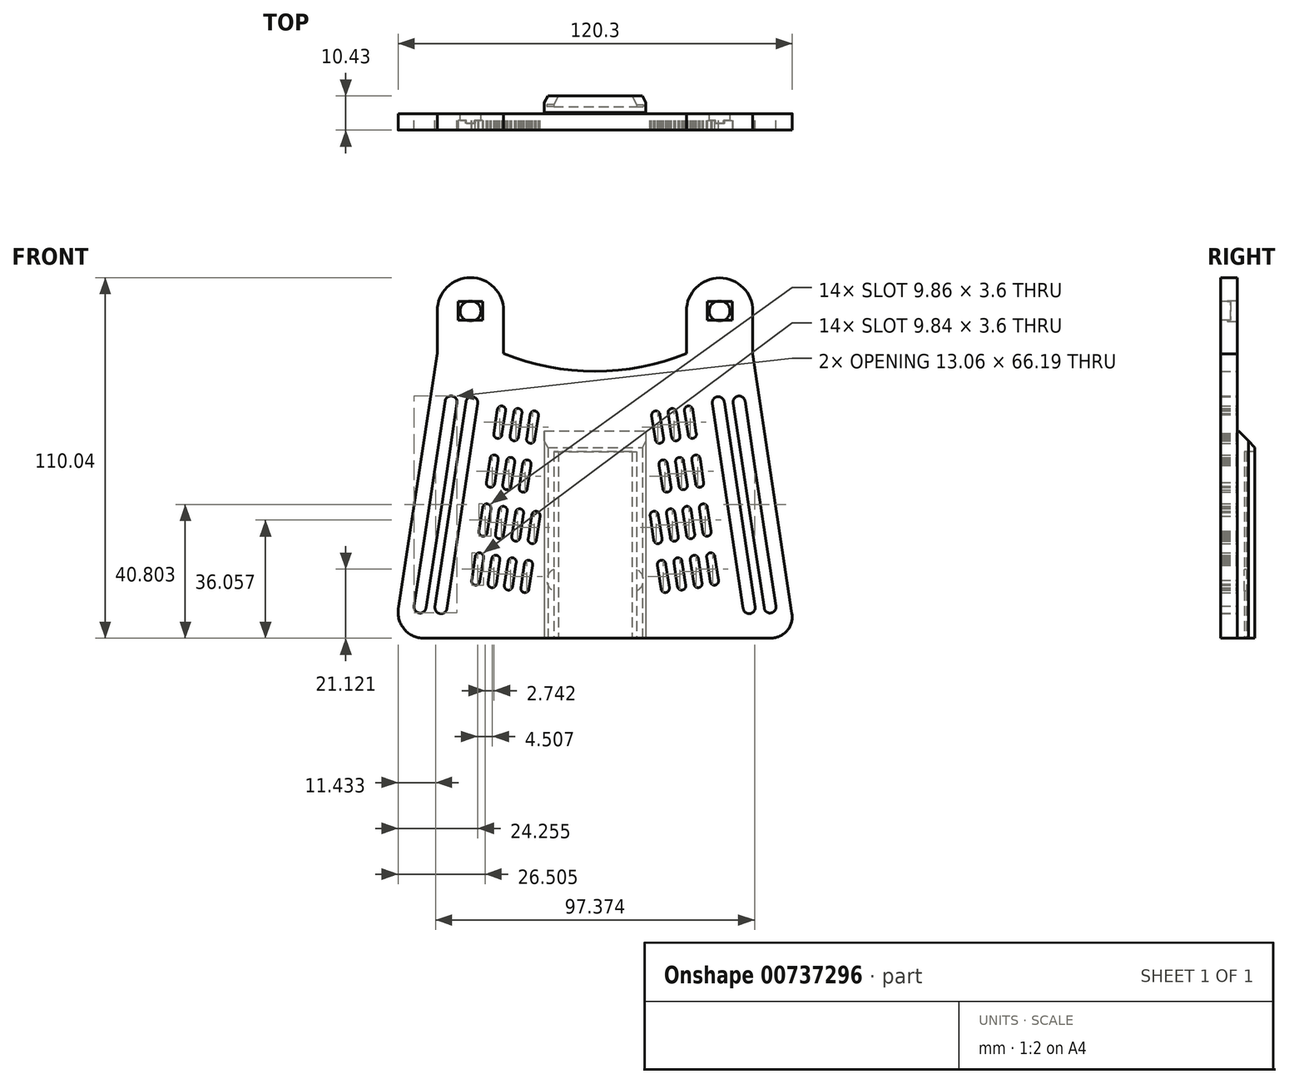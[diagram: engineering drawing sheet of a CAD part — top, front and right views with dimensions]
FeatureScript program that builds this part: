
annotation { "Feature Type Name" : "Feature", "Feature Type Description" : "" }
export const myFeature = defineFeature(function(context is Context, id is Id, definition is map)
    precondition{}
    {
        {
            assignVariable(context, id + "F0", {"name" : "thickness", "anyValue" : 4});
        }
        {
            var Q0;
            Q0=qCreatedBy(makeId("Front.planeOp"),FACE);
            var sketch = newSketch(context, id + "F1", { "sketchPlane" : qUnion([Q0])});
            skLineSegment(sketch, "E0", {"start": v(-22.08, 35.56) * mm, "end": v(-22.08, 25.27) * mm});
            skLineSegment(sketch, "E1", {"start": v(-38.08, 35.56) * mm, "end": v(-38.08, 25.41) * mm});
            skLineSegment(sketch, "E2", {"start": v(-38.08, 25.41) * mm, "end": v(-47.46, -36.33) * mm});
            skLineSegment(sketch, "E3", {"start": v(-41.36, -43.42) * mm, "end": v(42.4, -43.42) * mm});
            skLineSegment(sketch, "E4", {"start": v(47.52, -37.48) * mm, "end": v(38.06, 25.2) * mm});
            skLineSegment(sketch, "E5", {"start": v(38.06, 25.2) * mm, "end": v(38.06, 35.5) * mm});
            skLineSegment(sketch, "E6", {"start": v(22.06, 35.5) * mm, "end": v(22.06, 25.26) * mm});
            skArc(sketch, "E7", {"start": v(-22.08, 25.27) * mm, "mid": v(0, 21) * mm, "end": v(22.06, 25.26) * mm});
            skCircle(sketch, "E8", {"center": v(-30.08, 35.56) * mm, "radius": 8 * mm});
            skPoint(sketch, "E8.first.point", {"position": v(-30.38, 43.56) * mm});
            skCircle(sketch, "E9", {"center": v(30.06, 35.5) * mm, "radius": 8 * mm});
            skPoint(sketch, "E9.second.point", {"position": v(29.54, 43.49) * mm});
            skArc(sketch, "E10", {"start": v(47.52, -37.48) * mm, "mid": v(46.33, -41.63) * mm, "end": v(42.4, -43.42) * mm});
            skArc(sketch, "E11", {"start": v(-47.46, -36.33) * mm, "mid": v(-46.04, -41.28) * mm, "end": v(-41.36, -43.42) * mm});
            skLineSegment(sketch, "E12", {"start": v(0, 64.8) * mm, "end": v(0, 21) * mm, "construction": true});
            skLineSegment(sketch, "E13", {"start": v(0, 21) * mm, "end": v(0, -58.54) * mm, "construction": true});
            skCircle(sketch, "E14", {"center": v(34.76, 13.56) * mm, "radius": 1.45 * mm});
            skPoint(sketch, "E14.first.point", {"position": v(33.33, 13.34) * mm});
            skPoint(sketch, "E14.second.point", {"position": v(34.45, 14.97) * mm});
            skPoint(sketch, "E14.third.point", {"position": v(36.2, 13.77) * mm});
            skPoint(sketch, "E15.first.point", {"position": v(35.7, -2.5) * mm});
            skPoint(sketch, "E15.second.point", {"position": v(38.57, -2.07) * mm});
            skPoint(sketch, "E16.first.point", {"position": v(38.32, -19.78) * mm});
            skPoint(sketch, "E16.third.point", {"position": v(41.17, -19.34) * mm});
            skLineSegment(sketch, "E17", {"start": v(43.34, -43.34) * mm, "end": v(30.24, 43.5) * mm, "construction": true});
            skCircle(sketch, "E18", {"center": v(42.23, -35.9) * mm, "radius": 1.45 * mm});
            skPoint(sketch, "E18.first.point", {"position": v(40.8, -36.12) * mm});
            skPoint(sketch, "E18.second.point", {"position": v(42.44, -37.33) * mm});
            skPoint(sketch, "E18.third.point", {"position": v(43.67, -35.74) * mm});
            skLineSegment(sketch, "E19", {"start": v(36.2, 13.77) * mm, "end": v(38.57, -2.07) * mm});
            skLineSegment(sketch, "E20", {"start": v(33.33, 13.34) * mm, "end": v(35.7, -2.5) * mm});
            skLineSegment(sketch, "E21", {"start": v(38.32, -19.78) * mm, "end": v(40.8, -36.12) * mm});
            skLineSegment(sketch, "E22", {"start": v(41.17, -19.34) * mm, "end": v(43.67, -35.74) * mm});
            skLineSegment(sketch, "E23", {"start": v(41.17, -19.34) * mm, "end": v(38.57, -2.07) * mm});
            skLineSegment(sketch, "E24", {"start": v(38.32, -19.78) * mm, "end": v(35.7, -2.5) * mm});
            skLineSegment(sketch, "E25", {"start": v(30.88, -43.42) * mm, "end": v(20.6, 24.7) * mm, "construction": true});
            skCircle(sketch, "E26", {"center": v(28.8, -29.63) * mm, "radius": 1 * mm});
            skLineSegment(sketch, "E27", {"start": v(26.92, -23.82) * mm, "end": v(27.8, -29.78) * mm});
            skLineSegment(sketch, "E28", {"start": v(28.9, -23.6) * mm, "end": v(29.8, -29.53) * mm});
            skCircle(sketch, "E29", {"center": v(27.92, -23.82) * mm, "radius": 1 * mm});
            skLineSegment(sketch, "E30", {"start": v(29.25, -32.63) * mm, "end": v(35.1, -31.75) * mm, "construction": true});
            skLineSegment(sketch, "E31", {"start": v(27.47, -20.82) * mm, "end": v(32.3, -20.1) * mm, "construction": true});
            skCircle(sketch, "E32.MirrorC", {"center": v(24.36, -0.2) * mm, "radius": 1 * mm});
            skLineSegment(sketch, "E33.MirrorCS", {"start": v(25.33, 0.02) * mm, "end": v(26.23, -5.91) * mm});
            skLineSegment(sketch, "E34.MirrorCS", {"start": v(23.36, -0.2) * mm, "end": v(24.24, -6.16) * mm});
            skCircle(sketch, "E35.MirrorC", {"center": v(25.23, -6.01) * mm, "radius": 1 * mm});
            skCircle(sketch, "E36.MirrorC", {"center": v(27.01, -17.82) * mm, "radius": 1 * mm});
            skCircle(sketch, "E37.MirrorC", {"center": v(26.14, -12.01) * mm, "radius": 1 * mm});
            skLineSegment(sketch, "E38.MirrorCS", {"start": v(26.06, -18.12) * mm, "end": v(25.15, -12.17) * mm});
            skLineSegment(sketch, "E39.MirrorCS", {"start": v(28.01, -17.75) * mm, "end": v(27.12, -11.82) * mm});
            skLineSegment(sketch, "E40", {"start": v(23.9, 2.8) * mm, "end": v(29.03, 3.57) * mm, "construction": true});
            skCircle(sketch, "E41.MirrorC", {"center": v(22.58, 11.6) * mm, "radius": 1 * mm});
            skCircle(sketch, "E42.MirrorC", {"center": v(23.45, 5.8) * mm, "radius": 1 * mm});
            skLineSegment(sketch, "E43.MirrorCS", {"start": v(24.45, 5.86) * mm, "end": v(23.56, 11.8) * mm});
            skLineSegment(sketch, "E44.MirrorCS", {"start": v(22.5, 5.5) * mm, "end": v(21.59, 11.45) * mm});
            skCircle(sketch, "E45", {"center": v(29.73, 13.4) * mm, "radius": 1.45 * mm});
            skPoint(sketch, "E45.first.point", {"position": v(28.3, 13.18) * mm});
            skPoint(sketch, "E45.second.point", {"position": v(29.41, 14.81) * mm});
            skPoint(sketch, "E45.third.point", {"position": v(31.16, 13.61) * mm});
            skLineSegment(sketch, "E46", {"start": v(38.31, -43.5) * mm, "end": v(25.21, 43.34) * mm, "construction": true});
            skCircle(sketch, "E47", {"center": v(37.2, -36.06) * mm, "radius": 1.45 * mm});
            skLineSegment(sketch, "E48", {"start": v(28.85, -43.42) * mm, "end": v(18.68, 24.02) * mm, "construction": true});
            skCircle(sketch, "E49.MirrorC", {"center": v(22.18, -12.61) * mm, "radius": 1 * mm});
            skCircle(sketch, "E50.MirrorC", {"center": v(21.28, -6.61) * mm, "radius": 1 * mm});
            skCircle(sketch, "E51.MirrorC", {"center": v(18.62, 11) * mm, "radius": 1 * mm});
            skCircle(sketch, "E52.MirrorC", {"center": v(19.5, 5.2) * mm, "radius": 1 * mm});
            skLineSegment(sketch, "E53.MirrorCS", {"start": v(18.52, 4.97) * mm, "end": v(17.63, 10.9) * mm});
            skLineSegment(sketch, "E54.MirrorCS", {"start": v(19.95, 2.2) * mm, "end": v(14.82, 1.42) * mm, "construction": true});
            skLineSegment(sketch, "E55.MirrorCS", {"start": v(25.3, -33.23) * mm, "end": v(19.45, -34.1) * mm, "construction": true});
            skCircle(sketch, "E56.MirrorC", {"center": v(20.4, -0.8) * mm, "radius": 1 * mm});
            skCircle(sketch, "E57.MirrorC", {"center": v(23.96, -24.42) * mm, "radius": 1 * mm});
            skLineSegment(sketch, "E58.MirrorCS", {"start": v(26.92, -44.02) * mm, "end": v(16.64, 24.1) * mm, "construction": true});
            skLineSegment(sketch, "E59.MirrorCS", {"start": v(23.51, -21.42) * mm, "end": v(18.69, -22.15) * mm, "construction": true});
            skCircle(sketch, "E60.MirrorC", {"center": v(23.06, -18.42) * mm, "radius": 1 * mm});
            skCircle(sketch, "E61.MirrorC", {"center": v(24.84, -30.23) * mm, "radius": 1 * mm});
            skLineSegment(sketch, "E62.MirrorCS", {"start": v(19.4, -0.87) * mm, "end": v(20.3, -6.8) * mm});
            skLineSegment(sketch, "E63.MirrorCS", {"start": v(21.36, -0.5) * mm, "end": v(22.27, -6.46) * mm});
            skLineSegment(sketch, "E64.MirrorCS", {"start": v(24.92, -24.12) * mm, "end": v(25.83, -30.07) * mm});
            skLineSegment(sketch, "E65.MirrorCS", {"start": v(20.5, 5.2) * mm, "end": v(19.6, 11.15) * mm});
            skLineSegment(sketch, "E66.MirrorCS", {"start": v(22.97, -24.49) * mm, "end": v(23.86, -30.42) * mm});
            skLineSegment(sketch, "E67.MirrorCS", {"start": v(24.06, -18.42) * mm, "end": v(23.17, -12.46) * mm});
            skLineSegment(sketch, "E68.MirrorCS", {"start": v(22.09, -18.65) * mm, "end": v(21.19, -12.71) * mm});
            skLineSegment(sketch, "E69", {"start": v(28.3, 13.18) * mm, "end": v(35.76, -36.28) * mm});
            skLineSegment(sketch, "E70", {"start": v(31.16, 13.61) * mm, "end": v(38.62, -35.85) * mm});
            skLineSegment(sketch, "E71", {"start": v(14.8, 22.88) * mm, "end": v(24.8, -43.42) * mm, "construction": true});
            skCircle(sketch, "E72.MirrorC", {"center": v(18.23, -13.2) * mm, "radius": 1 * mm});
            skCircle(sketch, "E73.MirrorC", {"center": v(16.45, -1.4) * mm, "radius": 1 * mm});
            skCircle(sketch, "E74.MirrorC", {"center": v(14.67, 10.4) * mm, "radius": 1 * mm});
            skCircle(sketch, "E75.MirrorC", {"center": v(15.54, 4.6) * mm, "radius": 1 * mm});
            skCircle(sketch, "E76.MirrorC", {"center": v(20.89, -30.82) * mm, "radius": 1 * mm});
            skCircle(sketch, "E77.MirrorC", {"center": v(20, -25.02) * mm, "radius": 1 * mm});
            skLineSegment(sketch, "E78.MirrorCS", {"start": v(15.6, -22.61) * mm, "end": v(10.78, -23.34) * mm, "construction": true});
            skCircle(sketch, "E79.MirrorC", {"center": v(19.1, -19.02) * mm, "radius": 1 * mm});
            skCircle(sketch, "E80.MirrorC", {"center": v(14.27, -13.8) * mm, "radius": 1 * mm});
            skCircle(sketch, "E81.MirrorC", {"center": v(16.93, -31.42) * mm, "radius": 1 * mm});
            skCircle(sketch, "E82.MirrorC", {"center": v(15.15, -19.61) * mm, "radius": 1 * mm});
            skCircle(sketch, "E83.MirrorC", {"center": v(16.05, -25.61) * mm, "radius": 1 * mm});
            skCircle(sketch, "E84.MirrorC", {"center": v(17.32, -7.2) * mm, "radius": 1 * mm});
            skLineSegment(sketch, "E85.MirrorCS", {"start": v(17, -25.32) * mm, "end": v(17.92, -31.27) * mm});
            skLineSegment(sketch, "E86.MirrorCS", {"start": v(20.1, -18.95) * mm, "end": v(19.2, -13.01) * mm});
            skLineSegment(sketch, "E87.MirrorCS", {"start": v(14.18, -19.84) * mm, "end": v(13.28, -13.9) * mm});
            skLineSegment(sketch, "E88.MirrorCS", {"start": v(18.15, -19.31) * mm, "end": v(17.24, -13.36) * mm});
            skLineSegment(sketch, "E89.MirrorCS", {"start": v(16.15, -19.61) * mm, "end": v(15.26, -13.66) * mm});
            skLineSegment(sketch, "E90.MirrorCS", {"start": v(16, 1.6) * mm, "end": v(21.12, 2.37) * mm, "construction": true});
            skLineSegment(sketch, "E91.MirrorCS", {"start": v(15.45, -1.4) * mm, "end": v(16.33, -7.36) * mm});
            skLineSegment(sketch, "E92.MirrorCS", {"start": v(19, -25.02) * mm, "end": v(19.9, -30.97) * mm});
            skLineSegment(sketch, "E93.MirrorCS", {"start": v(14.59, 4.3) * mm, "end": v(13.68, 10.25) * mm});
            skLineSegment(sketch, "E94.MirrorCS", {"start": v(19.56, -22.02) * mm, "end": v(24.38, -21.29) * mm, "construction": true});
            skLineSegment(sketch, "E95.MirrorCS", {"start": v(20.98, -24.79) * mm, "end": v(21.88, -30.72) * mm});
            skLineSegment(sketch, "E96.MirrorCS", {"start": v(15.06, -25.68) * mm, "end": v(15.95, -31.61) * mm});
            skLineSegment(sketch, "E97.MirrorCS", {"start": v(17.42, -1.17) * mm, "end": v(18.32, -7.1) * mm});
            skLineSegment(sketch, "E98.MirrorCS", {"start": v(19.01, -45.21) * mm, "end": v(8.73, 22.9) * mm, "construction": true});
            skLineSegment(sketch, "E99.MirrorCS", {"start": v(12.04, 1) * mm, "end": v(6.91, 0.23) * mm, "construction": true});
            skLineSegment(sketch, "E100.MirrorCS", {"start": v(16.54, 4.67) * mm, "end": v(15.65, 10.6) * mm});
            skLineSegment(sketch, "E101.MirrorCS", {"start": v(21.34, -33.82) * mm, "end": v(27.18, -32.94) * mm, "construction": true});
            skLineSegment(sketch, "E102.MirrorCS", {"start": v(17.38, -34.42) * mm, "end": v(11.54, -35.3) * mm, "construction": true});
            skLineSegment(sketch, "E103.MirrorCS", {"start": v(22.97, -44.62) * mm, "end": v(12.69, 23.5) * mm, "construction": true});
            skLineSegment(sketch, "E104.MirrorCS", {"start": v(20.94, -44.62) * mm, "end": v(10.77, 22.83) * mm, "construction": true});
            skCircle(sketch, "E105.MirrorC", {"center": v(-29.73, 13.4) * mm, "radius": 1.45 * mm});
            skPoint(sketch, "E106.MirrorP", {"position": v(-29.41, 14.81) * mm});
            skCircle(sketch, "E107.MirrorC", {"center": v(-34.76, 13.56) * mm, "radius": 1.45 * mm});
            skCircle(sketch, "E108.MirrorC", {"center": v(-16.05, -25.61) * mm, "radius": 1 * mm});
            skCircle(sketch, "E109.MirrorC", {"center": v(-16.93, -31.42) * mm, "radius": 1 * mm});
            skCircle(sketch, "E110.MirrorC", {"center": v(-20.89, -30.82) * mm, "radius": 1 * mm});
            skLineSegment(sketch, "E111.MirrorCS", {"start": v(-19, -25.02) * mm, "end": v(-19.9, -30.97) * mm});
            skLineSegment(sketch, "E112.MirrorCS", {"start": v(-17, -25.32) * mm, "end": v(-17.92, -31.27) * mm});
            skLineSegment(sketch, "E113.MirrorCS", {"start": v(-15.06, -25.68) * mm, "end": v(-15.95, -31.61) * mm});
            skCircle(sketch, "E114.MirrorC", {"center": v(-15.15, -19.61) * mm, "radius": 1 * mm});
            skLineSegment(sketch, "E115.MirrorCS", {"start": v(-16.15, -19.61) * mm, "end": v(-15.26, -13.66) * mm});
            skLineSegment(sketch, "E116.MirrorCS", {"start": v(-14.18, -19.84) * mm, "end": v(-13.28, -13.9) * mm});
            skCircle(sketch, "E117.MirrorC", {"center": v(-42.23, -35.9) * mm, "radius": 1.45 * mm});
            skPoint(sketch, "E118.MirrorP", {"position": v(-43.67, -35.74) * mm});
            skLineSegment(sketch, "E119.MirrorCS", {"start": v(-33.33, 13.34) * mm, "end": v(-35.7, -2.5) * mm});
            skLineSegment(sketch, "E120.MirrorCS", {"start": v(-36.2, 13.77) * mm, "end": v(-38.57, -2.07) * mm});
            skLineSegment(sketch, "E121.MirrorCS", {"start": v(-41.17, -19.34) * mm, "end": v(-38.57, -2.07) * mm});
            skCircle(sketch, "E122.MirrorC", {"center": v(-14.27, -13.8) * mm, "radius": 1 * mm});
            skCircle(sketch, "E123.MirrorC", {"center": v(-15.54, 4.6) * mm, "radius": 1 * mm});
            skCircle(sketch, "E124.MirrorC", {"center": v(-22.58, 11.6) * mm, "radius": 1 * mm});
            skCircle(sketch, "E125.MirrorC", {"center": v(-25.23, -6.01) * mm, "radius": 1 * mm});
            skCircle(sketch, "E126.MirrorC", {"center": v(-24.36, -0.2) * mm, "radius": 1 * mm});
            skCircle(sketch, "E127.MirrorC", {"center": v(-19.1, -19.02) * mm, "radius": 1 * mm});
            skCircle(sketch, "E128.MirrorC", {"center": v(-28.8, -29.63) * mm, "radius": 1 * mm});
            skCircle(sketch, "E129.MirrorC", {"center": v(-23.96, -24.42) * mm, "radius": 1 * mm});
            skCircle(sketch, "E130.MirrorC", {"center": v(-17.32, -7.2) * mm, "radius": 1 * mm});
            skCircle(sketch, "E131.MirrorC", {"center": v(-20.4, -0.8) * mm, "radius": 1 * mm});
            skCircle(sketch, "E132.MirrorC", {"center": v(-26.14, -12.01) * mm, "radius": 1 * mm});
            skCircle(sketch, "E133.MirrorC", {"center": v(-23.06, -18.42) * mm, "radius": 1 * mm});
            skCircle(sketch, "E134.MirrorC", {"center": v(-27.92, -23.82) * mm, "radius": 1 * mm});
            skCircle(sketch, "E135.MirrorC", {"center": v(-24.84, -30.23) * mm, "radius": 1 * mm});
            skCircle(sketch, "E136.MirrorC", {"center": v(-21.28, -6.61) * mm, "radius": 1 * mm});
            skCircle(sketch, "E137.MirrorC", {"center": v(-18.23, -13.2) * mm, "radius": 1 * mm});
            skCircle(sketch, "E138.MirrorC", {"center": v(-14.67, 10.4) * mm, "radius": 1 * mm});
            skCircle(sketch, "E139.MirrorC", {"center": v(-22.18, -12.61) * mm, "radius": 1 * mm});
            skCircle(sketch, "E140.MirrorC", {"center": v(-23.45, 5.8) * mm, "radius": 1 * mm});
            skCircle(sketch, "E141.MirrorC", {"center": v(-37.2, -36.06) * mm, "radius": 1.45 * mm});
            skCircle(sketch, "E142.MirrorC", {"center": v(-18.62, 11) * mm, "radius": 1 * mm});
            skCircle(sketch, "E143.MirrorC", {"center": v(-20, -25.02) * mm, "radius": 1 * mm});
            skCircle(sketch, "E144.MirrorC", {"center": v(-16.45, -1.4) * mm, "radius": 1 * mm});
            skCircle(sketch, "E145.MirrorC", {"center": v(-27.01, -17.82) * mm, "radius": 1 * mm});
            skCircle(sketch, "E146.MirrorC", {"center": v(-19.5, 5.2) * mm, "radius": 1 * mm});
            skLineSegment(sketch, "E147.MirrorCS", {"start": v(-16.54, 4.67) * mm, "end": v(-15.65, 10.6) * mm});
            skLineSegment(sketch, "E148.MirrorCS", {"start": v(-28.01, -17.75) * mm, "end": v(-27.12, -11.82) * mm});
            skLineSegment(sketch, "E149.MirrorCS", {"start": v(-14.59, 4.3) * mm, "end": v(-13.68, 10.25) * mm});
            skLineSegment(sketch, "E150.MirrorCS", {"start": v(-18.15, -19.31) * mm, "end": v(-17.24, -13.36) * mm});
            skLineSegment(sketch, "E151.MirrorCS", {"start": v(-26.92, -23.82) * mm, "end": v(-27.8, -29.78) * mm});
            skLineSegment(sketch, "E152.MirrorCS", {"start": v(-24.45, 5.86) * mm, "end": v(-23.56, 11.8) * mm});
            skLineSegment(sketch, "E153.MirrorCS", {"start": v(-38.32, -19.78) * mm, "end": v(-35.7, -2.5) * mm});
            skLineSegment(sketch, "E154.MirrorCS", {"start": v(-24.06, -18.42) * mm, "end": v(-23.17, -12.46) * mm});
            skLineSegment(sketch, "E155.MirrorCS", {"start": v(-28.3, 13.18) * mm, "end": v(-35.76, -36.28) * mm});
            skLineSegment(sketch, "E156.MirrorCS", {"start": v(-31.16, 13.61) * mm, "end": v(-38.62, -35.85) * mm});
            skPoint(sketch, "E157.MirrorP", {"position": v(-41.17, -19.34) * mm});
            skLineSegment(sketch, "E158.MirrorCS", {"start": v(-24.92, -24.12) * mm, "end": v(-25.83, -30.07) * mm});
            skPoint(sketch, "E159.MirrorP", {"position": v(-38.32, -19.78) * mm});
            skLineSegment(sketch, "E160.MirrorCS", {"start": v(-25.33, 0.02) * mm, "end": v(-26.23, -5.91) * mm});
            skLineSegment(sketch, "E161.MirrorCS", {"start": v(-21.36, -0.5) * mm, "end": v(-22.27, -6.46) * mm});
            skLineSegment(sketch, "E162.MirrorCS", {"start": v(-17.42, -1.17) * mm, "end": v(-18.32, -7.1) * mm});
            skLineSegment(sketch, "E163.MirrorCS", {"start": v(-20.98, -24.79) * mm, "end": v(-21.88, -30.72) * mm});
            skLineSegment(sketch, "E164.MirrorCS", {"start": v(-38.32, -19.78) * mm, "end": v(-40.8, -36.12) * mm});
            skLineSegment(sketch, "E165.MirrorCS", {"start": v(-20.1, -18.95) * mm, "end": v(-19.2, -13.01) * mm});
            skLineSegment(sketch, "E166.MirrorCS", {"start": v(-18.52, 4.97) * mm, "end": v(-17.63, 10.9) * mm});
            skLineSegment(sketch, "E167.MirrorCS", {"start": v(-19.4, -0.87) * mm, "end": v(-20.3, -6.8) * mm});
            skLineSegment(sketch, "E168.MirrorCS", {"start": v(-22.5, 5.5) * mm, "end": v(-21.59, 11.45) * mm});
            skLineSegment(sketch, "E169.MirrorCS", {"start": v(-28.9, -23.6) * mm, "end": v(-29.8, -29.53) * mm});
            skLineSegment(sketch, "E170.MirrorCS", {"start": v(-26.06, -18.12) * mm, "end": v(-25.15, -12.17) * mm});
            skLineSegment(sketch, "E171.MirrorCS", {"start": v(-41.17, -19.34) * mm, "end": v(-43.67, -35.74) * mm});
            skLineSegment(sketch, "E172.MirrorCS", {"start": v(-22.97, -24.49) * mm, "end": v(-23.86, -30.42) * mm});
            skLineSegment(sketch, "E173.MirrorCS", {"start": v(-15.45, -1.4) * mm, "end": v(-16.33, -7.36) * mm});
            skLineSegment(sketch, "E174.MirrorCS", {"start": v(-23.36, -0.2) * mm, "end": v(-24.24, -6.16) * mm});
            skLineSegment(sketch, "E175.MirrorCS", {"start": v(-20.5, 5.2) * mm, "end": v(-19.6, 11.15) * mm});
            skLineSegment(sketch, "E176.MirrorCS", {"start": v(-22.09, -18.65) * mm, "end": v(-21.19, -12.71) * mm});
            skSolve(sketch);
        }
        {
            var Q0;
            {var subQ19=sQuery(id+"F1.wireOp",EDGE,"E0");Q0=makeQuery(id+"F1.imprint","IMPRINT",FACE,{"disambiguationData":[TD([[makeQuery(id+"F1.imprint","IMPRINT",EDGE,{"derivedFrom":subQ19}),-1.0]])]});}
            var Q1;
            {var subQ0=sQuery(id+"F1.wireOp",EDGE,"E8");var subQ1=makeQuery(id+"F1.imprint","INTERSECT",VERTEX,{"derivedFrom":[sQuery(id+"F1.wireOp",EDGE,"E0"),subQ0]});Q1=makeQuery(id+"F1.imprint","IMPRINT",FACE,{"disambiguationData":[TD([[makeQuery(id+"F1.imprint","IMPRINT",EDGE,{"disambiguationData":[TD([[subQ1,-1.0]])],"derivedFrom":subQ0}),1.0]])]});}
            var Q2;
            {var subQ0=sQuery(id+"F1.wireOp",EDGE,"E9");var subQ1=makeQuery(id+"F1.imprint","INTERSECT",VERTEX,{"derivedFrom":[sQuery(id+"F1.wireOp",EDGE,"E5"),subQ0]});Q2=makeQuery(id+"F1.imprint","IMPRINT",FACE,{"disambiguationData":[TD([[makeQuery(id+"F1.imprint","IMPRINT",EDGE,{"disambiguationData":[TD([[subQ1,-1.0]])],"derivedFrom":subQ0}),1.0]])]});}
            extrude(context, id + "F2", {"entities" : qUnion([Q0, Q1, Q2]), "depth" : (getVariable(context, 'thickness')) * mm, "offsetDistance" : 25 * mm});
        }
        {
            var Q0;
            Q0=makeQuery(id+"F2.opExtrude","SWEPT_FACE",FACE,{"disambiguationData":[OSD([sQuery(id+"F1.wireOp",EDGE,"E3")])]});
            var sketch = newSketch(context, id + "F3", { "sketchPlane" : qUnion([Q0])});
            skLineSegment(sketch, "E177", {"start": v(0, -16.4) * mm, "end": v(0, 21.93) * mm, "construction": true});
            skLineSegment(sketch, "E178", {"start": v(0, 0) * mm, "end": v(12.28, 0) * mm});
            skLineSegment(sketch, "E179", {"start": v(12.28, 0) * mm, "end": v(12.28, -2.67) * mm});
            skLineSegment(sketch, "E180", {"start": v(12.28, -2.67) * mm, "end": v(11.41, -4.25) * mm});
            skLineSegment(sketch, "E181", {"start": v(11.41, -4.25) * mm, "end": v(8.87, -4.25) * mm});
            skLineSegment(sketch, "E182", {"start": v(8.87, -4.25) * mm, "end": v(10, -2.18) * mm});
            skLineSegment(sketch, "E183", {"start": v(10, -2.18) * mm, "end": v(10, -1.68) * mm});
            skLineSegment(sketch, "E184", {"start": v(10, -1.68) * mm, "end": v(0, -1.68) * mm});
            skLineSegment(sketch, "E185.MirrorCS", {"start": v(-10, -2.18) * mm, "end": v(-10, -1.68) * mm});
            skLineSegment(sketch, "E186.MirrorCS", {"start": v(0, 0) * mm, "end": v(-12.28, 0) * mm});
            skLineSegment(sketch, "E187.MirrorCS", {"start": v(-11.41, -4.25) * mm, "end": v(-8.87, -4.25) * mm});
            skLineSegment(sketch, "E188.MirrorCS", {"start": v(-10, -1.68) * mm, "end": v(0, -1.68) * mm});
            skLineSegment(sketch, "E189.MirrorCS", {"start": v(-12.28, 0) * mm, "end": v(-12.28, -2.67) * mm});
            skLineSegment(sketch, "E190.MirrorCS", {"start": v(-8.87, -4.25) * mm, "end": v(-10, -2.18) * mm});
            skLineSegment(sketch, "E191.MirrorCS", {"start": v(-12.28, -2.67) * mm, "end": v(-11.41, -4.25) * mm});
            skSolve(sketch);
        }
        {
            var Q0;
            Q0 = qSketchRegion(id + "F3", true);
            extrude(context, id + "F4", {"entities" : qUnion([Q0]), "operationType" : NewBodyOperationType.ADD, "oppositeDirection" : true, "depth" : 45 * mm, "offsetDistance" : 25 * mm});
        }
        {
            var Q0;
            Q0=makeQuery(id+"F4.opExtrude","CAP_FACE",FACE,{"disambiguationData":[OSD([sQuery(id+"F3.wireOp",EDGE,"E178"),sQuery(id+"F3.wireOp",EDGE,"E179"),sQuery(id+"F3.wireOp",EDGE,"E180"),sQuery(id+"F3.wireOp",EDGE,"E181"),sQuery(id+"F3.wireOp",EDGE,"E182"),sQuery(id+"F3.wireOp",EDGE,"E183"),sQuery(id+"F3.wireOp",EDGE,"E184"),sQuery(id+"F3.wireOp",EDGE,"E185.MirrorCS"),sQuery(id+"F3.wireOp",EDGE,"E186.MirrorCS"),sQuery(id+"F3.wireOp",EDGE,"E187.MirrorCS"),sQuery(id+"F3.wireOp",EDGE,"E188.MirrorCS"),sQuery(id+"F3.wireOp",EDGE,"E189.MirrorCS"),sQuery(id+"F3.wireOp",EDGE,"E190.MirrorCS"),sQuery(id+"F3.wireOp",EDGE,"E191.MirrorCS")])],"isStart":false});
            cPlane(context, id + "F5", {"entities" : qUnion([Q0]), "cplaneType" : CPlaneType.OFFSET, "offset" : 0 * mm, "oppositeDirection" : true, "width" : 150 * mm, "height" : 150 * mm});
        }
        {
            var Q0;
            Q0=qCreatedBy(id+"F5.planeOp",FACE);
            var sketch = newSketch(context, id + "F6", { "sketchPlane" : qUnion([Q0])});
            skLineSegment(sketch, "E192", {"start": v(12.28, 0) * mm, "end": v(12.28, 2.67) * mm});
            skLineSegment(sketch, "E193", {"start": v(12.28, 2.67) * mm, "end": v(11.41, 4.25) * mm});
            skLineSegment(sketch, "E194", {"start": v(11.41, 4.25) * mm, "end": v(8.87, 4.25) * mm});
            skLineSegment(sketch, "E195", {"start": v(8.87, 4.25) * mm, "end": v(10, 2.18) * mm});
            skLineSegment(sketch, "E196", {"start": v(-11.41, 4.25) * mm, "end": v(-8.87, 4.25) * mm});
            skLineSegment(sketch, "E197", {"start": v(-12.28, 2.67) * mm, "end": v(-11.41, 4.25) * mm});
            skLineSegment(sketch, "E198", {"start": v(-12.28, 0) * mm, "end": v(-12.28, 2.67) * mm});
            skLineSegment(sketch, "E199", {"start": v(-12.28, 0) * mm, "end": v(12.28, 0) * mm});
            skLineSegment(sketch, "E200", {"start": v(-8.87, 4.25) * mm, "end": v(8.87, 4.25) * mm});
            skSolve(sketch);
        }
        {
            var Q0;
            Q0=makeQuery(id+"F6.imprint","IMPRINT",FACE,{"disambiguationData":[TD([[makeQuery(id+"F6.imprint","IMPRINT",EDGE,{"derivedFrom":sQuery(id+"F6.wireOp",EDGE,"E192")}),1.0]])]});
            extrude(context, id + "F7", {"entities" : qUnion([Q0]), "operationType" : NewBodyOperationType.ADD, "depth" : 5 * mm, "offsetDistance" : 25 * mm});
        }
        {
            var Q0;
            Q0=makeQuery(id+"F7.opExtrude","CAP_EDGE",EDGE,{"disambiguationData":[OSD([sQuery(id+"F6.wireOp",EDGE,"E194"),sQuery(id+"F6.wireOp",EDGE,"E196"),sQuery(id+"F6.wireOp",EDGE,"E200")])],"isStart":false});
            chamfer(context, id + "F8", {"entities" : qUnion([Q0]), "width" : 4 * mm, "tangentPropagation" : true});
        }
        {
            var Q0;
            Q0=makeQuery(id+"F4.opExtrude","SWEPT_FACE",FACE,{"disambiguationData":[OSD([sQuery(id+"F3.wireOp",EDGE,"E184"),sQuery(id+"F3.wireOp",EDGE,"E188.MirrorCS")])]});
            var sketch = newSketch(context, id + "F9", { "sketchPlane" : qUnion([Q0])});
            skArc(sketch, "E201", {"start": v(-10, -26.81) * mm, "mid": v(-11.64, -29.42) * mm, "end": v(-10, -32.02) * mm});
            skLineSegment(sketch, "E202", {"start": v(0, -30.46) * mm, "end": v(0, -50.6) * mm, "construction": true});
            skPoint(sketch, "E202.startSnap0", {"position": v(0, -43.42) * mm});
            skArc(sketch, "E203.MirrorCS", {"start": v(10, -26.81) * mm, "mid": v(11.64, -29.42) * mm, "end": v(10, -32.02) * mm});
            skLineSegment(sketch, "E204.MirrorCS", {"start": v(-20, -30.46) * mm, "end": v(-20, -50.6) * mm, "construction": true});
            skLineSegment(sketch, "E205", {"start": v(-10, -32.02) * mm, "end": v(-10, -26.81) * mm});
            skLineSegment(sketch, "E206", {"start": v(10, -32.02) * mm, "end": v(10, -26.81) * mm});
            skSolve(sketch);
        }
        {
            var Q0;
            Q0 = qSketchRegion(id + "F9", true);
            extrude(context, id + "F10", {"entities" : qUnion([Q0]), "operationType" : NewBodyOperationType.REMOVE, "depth" : 0.5 * mm, "hasOffset" : true, "offsetDistance" : 25 * mm});
        }
        {
            var Q0;
            Q0=makeQuery(id+"F2.opExtrude","CAP_FACE",FACE,{"disambiguationData":[OSD([sQuery(id+"F1.wireOp",EDGE,"E0"),sQuery(id+"F1.wireOp",EDGE,"E1"),sQuery(id+"F1.wireOp",EDGE,"E2"),sQuery(id+"F1.wireOp",EDGE,"E3"),sQuery(id+"F1.wireOp",EDGE,"E4"),sQuery(id+"F1.wireOp",EDGE,"E5"),sQuery(id+"F1.wireOp",EDGE,"E6"),sQuery(id+"F1.wireOp",EDGE,"E7"),sQuery(id+"F1.wireOp",EDGE,"E8"),sQuery(id+"F1.wireOp",EDGE,"E9"),sQuery(id+"F1.wireOp",EDGE,"E10"),sQuery(id+"F1.wireOp",EDGE,"E11"),sQuery(id+"F1.wireOp",EDGE,"9fce8818-836a-493b-a54f-37aa268f0d49"),sQuery(id+"F1.wireOp",EDGE,"83f0bc5a-3219-41d3-b34f-2fba7a032599"),sQuery(id+"F1.wireOp",EDGE,"2a7f7abe-a1c7-432f-a265-4317609dc02b"),sQuery(id+"F1.wireOp",EDGE,"E14"),sQuery(id+"F1.wireOp",EDGE,"E15"),sQuery(id+"F1.wireOp",EDGE,"E16"),sQuery(id+"F1.wireOp",EDGE,"d3438065-2e1b-40b0-85ae-f31694300b5d"),sQuery(id+"F1.wireOp",EDGE,"E18"),sQuery(id+"F1.wireOp",EDGE,"E19"),sQuery(id+"F1.wireOp",EDGE,"E20"),sQuery(id+"F1.wireOp",EDGE,"E21"),sQuery(id+"F1.wireOp",EDGE,"E22"),sQuery(id+"F1.wireOp",EDGE,"XM2iGyD3-syAj-tAYT-SD2o-Bk4WIWmVb2HS"),sQuery(id+"F1.wireOp",EDGE,"ivoixY1T-hHBG-MRNb-R92C-OnGa2GkEEtBp"),sQuery(id+"F1.wireOp",EDGE,"fHdlp6QL-jg5i-YtLk-NcsM-PrGqWgHsT9NE"),sQuery(id+"F1.wireOp",EDGE,"p496zow3-aHBK-O8vn-93MF-RNBD8pPvk2gB")])],"isStart":false});
            var sketch = newSketch(context, id + "F11", { "sketchPlane" : qUnion([Q0])});
            skLineSegment(sketch, "E207.bottom", {"start": v(-27.08, 37.81) * mm, "end": v(-33.08, 37.81) * mm});
            skLineSegment(sketch, "E207.top", {"start": v(-27.08, 33.31) * mm, "end": v(-33.08, 33.31) * mm});
            skLineSegment(sketch, "E207.left", {"start": v(-27.08, 37.81) * mm, "end": v(-27.08, 33.31) * mm});
            skLineSegment(sketch, "E207.right", {"start": v(-33.08, 37.81) * mm, "end": v(-33.08, 33.31) * mm});
            skPoint(sketch, "E207.middle", {"position": v(-30.08, 35.56) * mm});
            skLineSegment(sketch, "E208", {"start": v(0, 0) * mm, "end": v(0, 28.4) * mm, "construction": true});
            skPoint(sketch, "E209.MirrorP", {"position": v(30.08, 35.56) * mm});
            skLineSegment(sketch, "E210.MirrorCS", {"start": v(27.08, 37.81) * mm, "end": v(27.08, 33.31) * mm});
            skLineSegment(sketch, "E211.MirrorCS", {"start": v(27.08, 37.81) * mm, "end": v(33.08, 37.81) * mm});
            skLineSegment(sketch, "E212.MirrorCS", {"start": v(33.08, 37.81) * mm, "end": v(33.08, 33.31) * mm});
            skLineSegment(sketch, "E213.MirrorCS", {"start": v(27.08, 33.31) * mm, "end": v(33.08, 33.31) * mm});
            skSolve(sketch);
        }
        {
            var Q0;
            Q0 = qSketchRegion(id + "F11", true);
            extrude(context, id + "F12", {"entities" : qUnion([Q0]), "operationType" : NewBodyOperationType.REMOVE, "oppositeDirection" : true, "depth" : 2.4 * mm, "offsetDistance" : 25 * mm});
        }
        {
            var Q0;
            Q0=makeQuery(id+"F2.opExtrude","CAP_FACE",FACE,{"disambiguationData":[OSD([sQuery(id+"F1.wireOp",EDGE,"E0"),sQuery(id+"F1.wireOp",EDGE,"E1"),sQuery(id+"F1.wireOp",EDGE,"E2"),sQuery(id+"F1.wireOp",EDGE,"E3"),sQuery(id+"F1.wireOp",EDGE,"E4"),sQuery(id+"F1.wireOp",EDGE,"E5"),sQuery(id+"F1.wireOp",EDGE,"E6"),sQuery(id+"F1.wireOp",EDGE,"E7"),sQuery(id+"F1.wireOp",EDGE,"E8"),sQuery(id+"F1.wireOp",EDGE,"E9"),sQuery(id+"F1.wireOp",EDGE,"E10"),sQuery(id+"F1.wireOp",EDGE,"E11"),sQuery(id+"F1.wireOp",EDGE,"9fce8818-836a-493b-a54f-37aa268f0d49"),sQuery(id+"F1.wireOp",EDGE,"83f0bc5a-3219-41d3-b34f-2fba7a032599"),sQuery(id+"F1.wireOp",EDGE,"2a7f7abe-a1c7-432f-a265-4317609dc02b"),sQuery(id+"F1.wireOp",EDGE,"E14"),sQuery(id+"F1.wireOp",EDGE,"E15"),sQuery(id+"F1.wireOp",EDGE,"E16"),sQuery(id+"F1.wireOp",EDGE,"d3438065-2e1b-40b0-85ae-f31694300b5d"),sQuery(id+"F1.wireOp",EDGE,"E18"),sQuery(id+"F1.wireOp",EDGE,"E19"),sQuery(id+"F1.wireOp",EDGE,"E20"),sQuery(id+"F1.wireOp",EDGE,"E21"),sQuery(id+"F1.wireOp",EDGE,"E22"),sQuery(id+"F1.wireOp",EDGE,"XM2iGyD3-syAj-tAYT-SD2o-Bk4WIWmVb2HS"),sQuery(id+"F1.wireOp",EDGE,"ivoixY1T-hHBG-MRNb-R92C-OnGa2GkEEtBp"),sQuery(id+"F1.wireOp",EDGE,"fHdlp6QL-jg5i-YtLk-NcsM-PrGqWgHsT9NE"),sQuery(id+"F1.wireOp",EDGE,"p496zow3-aHBK-O8vn-93MF-RNBD8pPvk2gB")])],"isStart":true});
            var sketch = newSketch(context, id + "F13", { "sketchPlane" : qUnion([Q0])});
            skCircle(sketch, "E214", {"center": v(-30.06, 35.5) * mm, "radius": 2.5 * mm});
            skLineSegment(sketch, "E215", {"start": v(0, 0) * mm, "end": v(0, 39.9) * mm, "construction": true});
            skCircle(sketch, "E216.MirrorC", {"center": v(30.06, 35.5) * mm, "radius": 2.5 * mm});
            skSolve(sketch);
        }
        {
            var Q0;
            Q0 = qSketchRegion(id + "F13", true);
            extrude(context, id + "F14", {"entities" : qUnion([Q0]), "operationType" : NewBodyOperationType.REMOVE, "oppositeDirection" : true, "depth" : 2.4 * mm, "offsetDistance" : 25 * mm});
        }
        {
            var Q0;
            Q0=makeQuery(id+"F2.opExtrude","SWEPT_BODY",BODY,{"disambiguationData":[OSD([sQuery(id+"F1.wireOp",EDGE,"E0"),sQuery(id+"F1.wireOp",EDGE,"E1"),sQuery(id+"F1.wireOp",EDGE,"E2"),sQuery(id+"F1.wireOp",EDGE,"E3"),sQuery(id+"F1.wireOp",EDGE,"E4"),sQuery(id+"F1.wireOp",EDGE,"E5"),sQuery(id+"F1.wireOp",EDGE,"E6"),sQuery(id+"F1.wireOp",EDGE,"E7"),sQuery(id+"F1.wireOp",EDGE,"E8"),sQuery(id+"F1.wireOp",EDGE,"E9"),sQuery(id+"F1.wireOp",EDGE,"E10"),sQuery(id+"F1.wireOp",EDGE,"E11"),sQuery(id+"F1.wireOp",EDGE,"E14"),sQuery(id+"F1.wireOp",EDGE,"E18"),sQuery(id+"F1.wireOp",EDGE,"E19"),sQuery(id+"F1.wireOp",EDGE,"E20"),sQuery(id+"F1.wireOp",EDGE,"E21"),sQuery(id+"F1.wireOp",EDGE,"E22"),sQuery(id+"F1.wireOp",EDGE,"E23"),sQuery(id+"F1.wireOp",EDGE,"E24"),sQuery(id+"F1.wireOp",EDGE,"E26"),sQuery(id+"F1.wireOp",EDGE,"E27"),sQuery(id+"F1.wireOp",EDGE,"E28"),sQuery(id+"F1.wireOp",EDGE,"E29"),sQuery(id+"F1.wireOp",EDGE,"E32.MirrorC"),sQuery(id+"F1.wireOp",EDGE,"E33.MirrorCS"),sQuery(id+"F1.wireOp",EDGE,"E34.MirrorCS"),sQuery(id+"F1.wireOp",EDGE,"E35.MirrorC"),sQuery(id+"F1.wireOp",EDGE,"E36.MirrorC"),sQuery(id+"F1.wireOp",EDGE,"E37.MirrorC"),sQuery(id+"F1.wireOp",EDGE,"E38.MirrorCS"),sQuery(id+"F1.wireOp",EDGE,"E39.MirrorCS"),sQuery(id+"F1.wireOp",EDGE,"E41.MirrorC"),sQuery(id+"F1.wireOp",EDGE,"E42.MirrorC"),sQuery(id+"F1.wireOp",EDGE,"E43.MirrorCS"),sQuery(id+"F1.wireOp",EDGE,"E44.MirrorCS"),sQuery(id+"F1.wireOp",EDGE,"E45"),sQuery(id+"F1.wireOp",EDGE,"E47"),sQuery(id+"F1.wireOp",EDGE,"E49.MirrorC"),sQuery(id+"F1.wireOp",EDGE,"E50.MirrorC"),sQuery(id+"F1.wireOp",EDGE,"E51.MirrorC"),sQuery(id+"F1.wireOp",EDGE,"E52.MirrorC"),sQuery(id+"F1.wireOp",EDGE,"E53.MirrorCS"),sQuery(id+"F1.wireOp",EDGE,"E56.MirrorC"),sQuery(id+"F1.wireOp",EDGE,"E57.MirrorC"),sQuery(id+"F1.wireOp",EDGE,"E60.MirrorC"),sQuery(id+"F1.wireOp",EDGE,"E61.MirrorC"),sQuery(id+"F1.wireOp",EDGE,"E62.MirrorCS"),sQuery(id+"F1.wireOp",EDGE,"E63.MirrorCS"),sQuery(id+"F1.wireOp",EDGE,"E64.MirrorCS"),sQuery(id+"F1.wireOp",EDGE,"E65.MirrorCS"),sQuery(id+"F1.wireOp",EDGE,"E66.MirrorCS"),sQuery(id+"F1.wireOp",EDGE,"E67.MirrorCS"),sQuery(id+"F1.wireOp",EDGE,"E68.MirrorCS"),sQuery(id+"F1.wireOp",EDGE,"E69"),sQuery(id+"F1.wireOp",EDGE,"E70"),sQuery(id+"F1.wireOp",EDGE,"E72.MirrorC"),sQuery(id+"F1.wireOp",EDGE,"E73.MirrorC"),sQuery(id+"F1.wireOp",EDGE,"E74.MirrorC"),sQuery(id+"F1.wireOp",EDGE,"E75.MirrorC"),sQuery(id+"F1.wireOp",EDGE,"E76.MirrorC"),sQuery(id+"F1.wireOp",EDGE,"E77.MirrorC"),sQuery(id+"F1.wireOp",EDGE,"E79.MirrorC"),sQuery(id+"F1.wireOp",EDGE,"E80.MirrorC"),sQuery(id+"F1.wireOp",EDGE,"E81.MirrorC"),sQuery(id+"F1.wireOp",EDGE,"E82.MirrorC"),sQuery(id+"F1.wireOp",EDGE,"E83.MirrorC"),sQuery(id+"F1.wireOp",EDGE,"E84.MirrorC"),sQuery(id+"F1.wireOp",EDGE,"E85.MirrorCS"),sQuery(id+"F1.wireOp",EDGE,"E86.MirrorCS"),sQuery(id+"F1.wireOp",EDGE,"E87.MirrorCS"),sQuery(id+"F1.wireOp",EDGE,"E88.MirrorCS"),sQuery(id+"F1.wireOp",EDGE,"E89.MirrorCS"),sQuery(id+"F1.wireOp",EDGE,"E91.MirrorCS"),sQuery(id+"F1.wireOp",EDGE,"E92.MirrorCS"),sQuery(id+"F1.wireOp",EDGE,"E93.MirrorCS"),sQuery(id+"F1.wireOp",EDGE,"E95.MirrorCS"),sQuery(id+"F1.wireOp",EDGE,"E96.MirrorCS"),sQuery(id+"F1.wireOp",EDGE,"E97.MirrorCS"),sQuery(id+"F1.wireOp",EDGE,"E100.MirrorCS"),sQuery(id+"F1.wireOp",EDGE,"E105.MirrorC"),sQuery(id+"F1.wireOp",EDGE,"E107.MirrorC"),sQuery(id+"F1.wireOp",EDGE,"E108.MirrorC"),sQuery(id+"F1.wireOp",EDGE,"E109.MirrorC"),sQuery(id+"F1.wireOp",EDGE,"E110.MirrorC"),sQuery(id+"F1.wireOp",EDGE,"E111.MirrorCS"),sQuery(id+"F1.wireOp",EDGE,"E112.MirrorCS"),sQuery(id+"F1.wireOp",EDGE,"E113.MirrorCS"),sQuery(id+"F1.wireOp",EDGE,"E114.MirrorC"),sQuery(id+"F1.wireOp",EDGE,"E115.MirrorCS"),sQuery(id+"F1.wireOp",EDGE,"E116.MirrorCS"),sQuery(id+"F1.wireOp",EDGE,"E117.MirrorC"),sQuery(id+"F1.wireOp",EDGE,"E119.MirrorCS"),sQuery(id+"F1.wireOp",EDGE,"E120.MirrorCS"),sQuery(id+"F1.wireOp",EDGE,"E121.MirrorCS"),sQuery(id+"F1.wireOp",EDGE,"E122.MirrorC"),sQuery(id+"F1.wireOp",EDGE,"E123.MirrorC"),sQuery(id+"F1.wireOp",EDGE,"E124.MirrorC"),sQuery(id+"F1.wireOp",EDGE,"E125.MirrorC"),sQuery(id+"F1.wireOp",EDGE,"E126.MirrorC"),sQuery(id+"F1.wireOp",EDGE,"E127.MirrorC"),sQuery(id+"F1.wireOp",EDGE,"E128.MirrorC"),sQuery(id+"F1.wireOp",EDGE,"E129.MirrorC"),sQuery(id+"F1.wireOp",EDGE,"E130.MirrorC"),sQuery(id+"F1.wireOp",EDGE,"E131.MirrorC"),sQuery(id+"F1.wireOp",EDGE,"E132.MirrorC"),sQuery(id+"F1.wireOp",EDGE,"E133.MirrorC"),sQuery(id+"F1.wireOp",EDGE,"E134.MirrorC"),sQuery(id+"F1.wireOp",EDGE,"E135.MirrorC"),sQuery(id+"F1.wireOp",EDGE,"E136.MirrorC"),sQuery(id+"F1.wireOp",EDGE,"E137.MirrorC"),sQuery(id+"F1.wireOp",EDGE,"E138.MirrorC"),sQuery(id+"F1.wireOp",EDGE,"E139.MirrorC"),sQuery(id+"F1.wireOp",EDGE,"E140.MirrorC"),sQuery(id+"F1.wireOp",EDGE,"E141.MirrorC"),sQuery(id+"F1.wireOp",EDGE,"E142.MirrorC"),sQuery(id+"F1.wireOp",EDGE,"E143.MirrorC"),sQuery(id+"F1.wireOp",EDGE,"E144.MirrorC"),sQuery(id+"F1.wireOp",EDGE,"E145.MirrorC"),sQuery(id+"F1.wireOp",EDGE,"E146.MirrorC"),sQuery(id+"F1.wireOp",EDGE,"E147.MirrorCS"),sQuery(id+"F1.wireOp",EDGE,"E148.MirrorCS"),sQuery(id+"F1.wireOp",EDGE,"E149.MirrorCS"),sQuery(id+"F1.wireOp",EDGE,"E150.MirrorCS"),sQuery(id+"F1.wireOp",EDGE,"E151.MirrorCS"),sQuery(id+"F1.wireOp",EDGE,"E152.MirrorCS"),sQuery(id+"F1.wireOp",EDGE,"E153.MirrorCS"),sQuery(id+"F1.wireOp",EDGE,"E154.MirrorCS"),sQuery(id+"F1.wireOp",EDGE,"E155.MirrorCS"),sQuery(id+"F1.wireOp",EDGE,"E156.MirrorCS"),sQuery(id+"F1.wireOp",EDGE,"E158.MirrorCS"),sQuery(id+"F1.wireOp",EDGE,"E160.MirrorCS"),sQuery(id+"F1.wireOp",EDGE,"E161.MirrorCS"),sQuery(id+"F1.wireOp",EDGE,"E162.MirrorCS"),sQuery(id+"F1.wireOp",EDGE,"E163.MirrorCS"),sQuery(id+"F1.wireOp",EDGE,"E164.MirrorCS"),sQuery(id+"F1.wireOp",EDGE,"E165.MirrorCS"),sQuery(id+"F1.wireOp",EDGE,"E166.MirrorCS"),sQuery(id+"F1.wireOp",EDGE,"E167.MirrorCS"),sQuery(id+"F1.wireOp",EDGE,"E168.MirrorCS"),sQuery(id+"F1.wireOp",EDGE,"E169.MirrorCS"),sQuery(id+"F1.wireOp",EDGE,"E170.MirrorCS"),sQuery(id+"F1.wireOp",EDGE,"E171.MirrorCS"),sQuery(id+"F1.wireOp",EDGE,"E172.MirrorCS"),sQuery(id+"F1.wireOp",EDGE,"E173.MirrorCS"),sQuery(id+"F1.wireOp",EDGE,"E174.MirrorCS"),sQuery(id+"F1.wireOp",EDGE,"E175.MirrorCS"),sQuery(id+"F1.wireOp",EDGE,"E176.MirrorCS")])]});
            var Q1;
            Q1=qCreatedBy(makeId("Origin.pointOp"),VERTEX);
            transform(context, id + "F15", {"entities" : qUnion([Q0]), "transformType" : TransformType.SCALE_UNIFORMLY, "scale" : 1.1 * 1.15, "scalePoint" : qUnion([Q1]), "makeCopy" : false});
        }
    });
